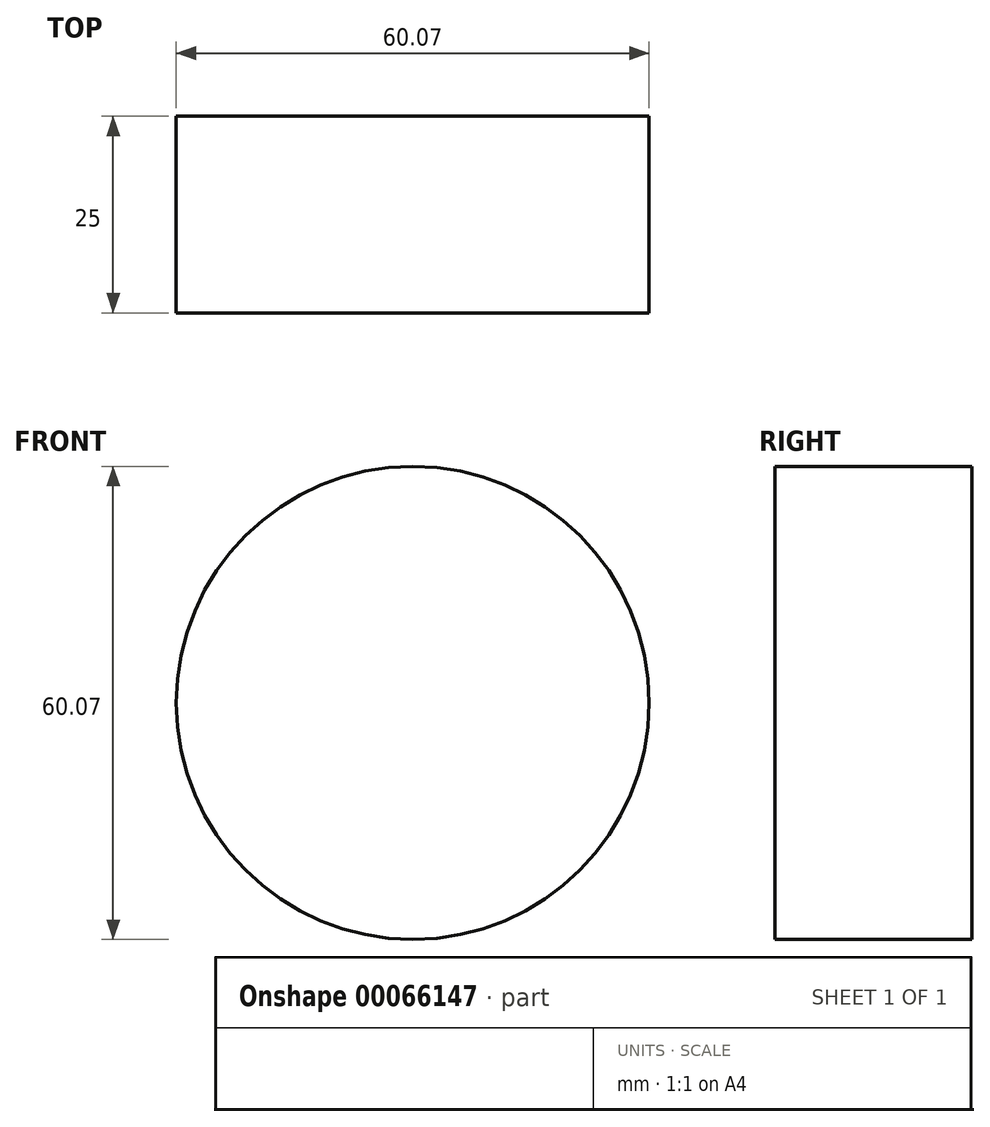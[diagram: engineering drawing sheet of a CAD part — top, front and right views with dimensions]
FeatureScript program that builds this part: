
annotation { "Feature Type Name" : "Feature", "Feature Type Description" : "" }
export const myFeature = defineFeature(function(context is Context, id is Id, definition is map)
    precondition{}
    {
        {
            var Q0;
            Q0=qCreatedBy(makeId("Front.planeOp"),FACE);
            var sketch = newSketch(context, id + "F0", { "sketchPlane" : qUnion([Q0])});
            skCircle(sketch, "E0", {"center": v(-40.6, 31.72) * mm, "radius": 30.04 * mm});
            skSolve(sketch);
        }
        {
            var Q0;
            Q0=makeQuery(id+"F0.imprint","IMPRINT",FACE,{"disambiguationData":[TD([[makeQuery(id+"F0.imprint","IMPRINT",EDGE,{"derivedFrom":sQuery(id+"F0.wireOp",EDGE,"E0")}),1.0]])]});
            extrude(context, id + "F1", {"entities" : qUnion([Q0]), "depth" : 25 * mm});
        }
    });
